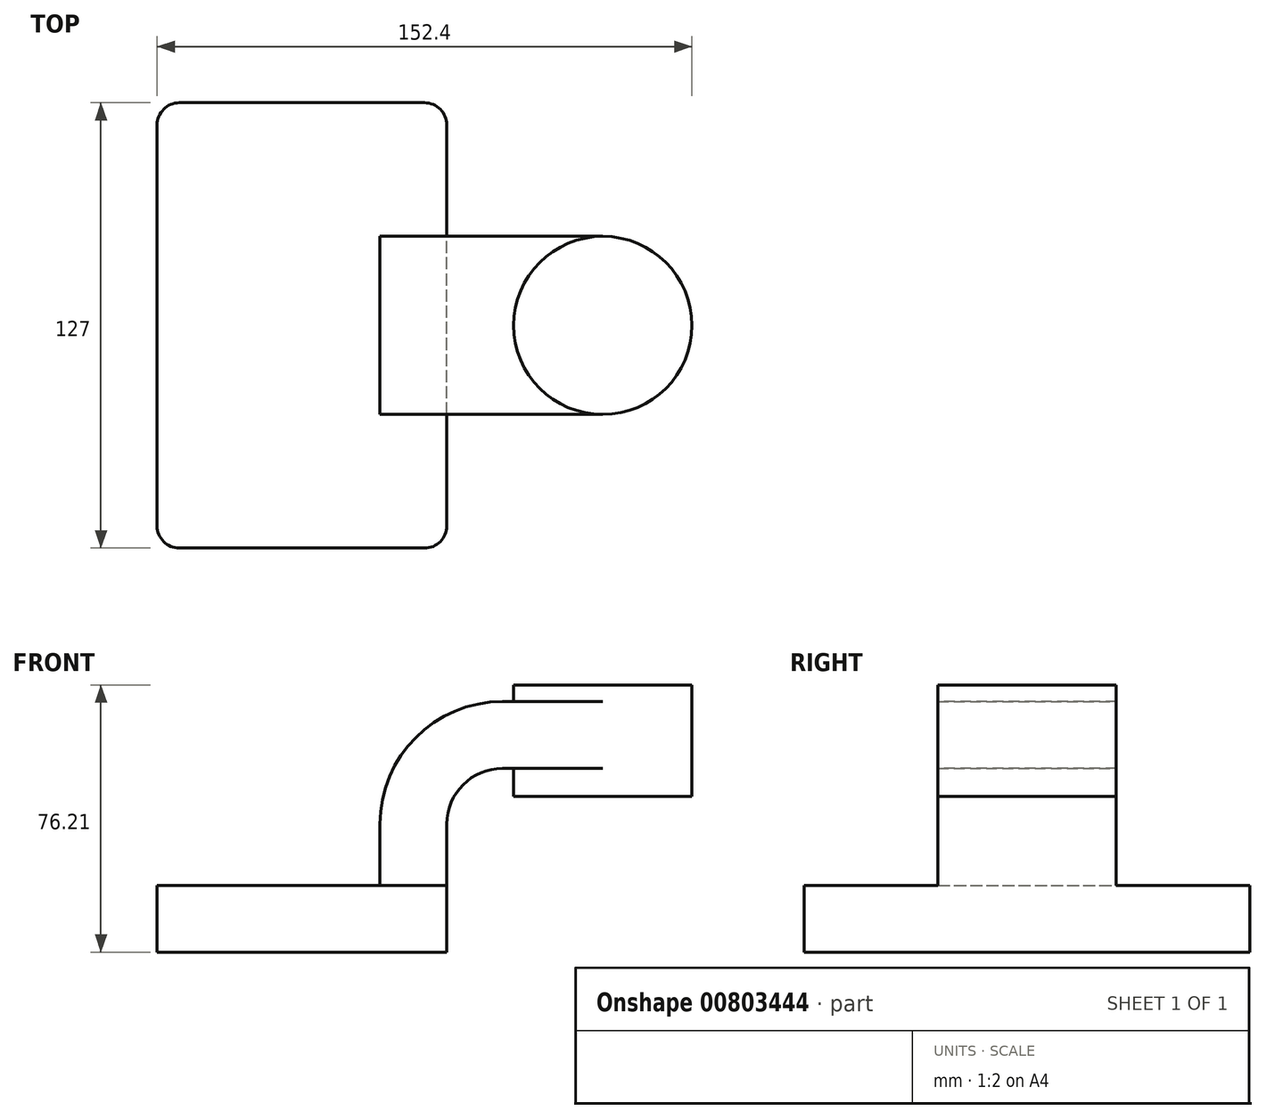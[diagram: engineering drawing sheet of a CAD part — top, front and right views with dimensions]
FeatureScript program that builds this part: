
annotation { "Feature Type Name" : "Feature", "Feature Type Description" : "" }
export const myFeature = defineFeature(function(context is Context, id is Id, definition is map)
    precondition{}
    {
        {
            var Q0;
            Q0=qCreatedBy(makeId("Front.planeOp"),FACE);
            var sketch = newSketch(context, id + "F0", { "sketchPlane" : qUnion([Q0])});
            skLineSegment(sketch, "E0.bottom", {"start": v(41.27, 9.53) * mm, "end": v(-41.28, 9.53) * mm});
            skLineSegment(sketch, "E0.top", {"start": v(41.28, -9.52) * mm, "end": v(-41.27, -9.52) * mm});
            skLineSegment(sketch, "E0.left", {"start": v(41.28, 9.53) * mm, "end": v(41.28, -9.52) * mm});
            skLineSegment(sketch, "E0.right", {"start": v(-41.28, 9.53) * mm, "end": v(-41.27, -9.52) * mm});
            skPoint(sketch, "E0.middle", {"position": v(0, 0) * mm});
            skLineSegment(sketch, "E1.bottom", {"start": v(111.13, 34.93) * mm, "end": v(60.33, 34.93) * mm});
            skLineSegment(sketch, "E1.top", {"start": v(111.13, 66.68) * mm, "end": v(60.33, 66.68) * mm});
            skLineSegment(sketch, "E1.left", {"start": v(111.13, 34.93) * mm, "end": v(111.13, 66.68) * mm});
            skLineSegment(sketch, "E1.right", {"start": v(60.33, 34.92) * mm, "end": v(60.33, 66.68) * mm});
            skPoint(sketch, "E1.middle", {"position": v(85.73, 50.8) * mm});
            skLineSegment(sketch, "E2", {"start": v(41.27, 9.53) * mm, "end": v(41.27, 26.99) * mm});
            skLineSegment(sketch, "E3", {"start": v(57.15, 42.86) * mm, "end": v(85.73, 42.86) * mm});
            skArc(sketch, "E4", {"start": v(41.27, 26.99) * mm, "mid": v(45.92, 38.21) * mm, "end": v(57.15, 42.86) * mm});
            skLineSegment(sketch, "E5.0", {"start": v(57.15, 61.91) * mm, "end": v(85.73, 61.91) * mm});
            skArc(sketch, "E5.1", {"start": v(22.22, 26.99) * mm, "mid": v(32.45, 51.68) * mm, "end": v(57.15, 61.91) * mm});
            skLineSegment(sketch, "E5.2", {"start": v(22.22, 9.53) * mm, "end": v(22.22, 26.99) * mm});
            skPoint(sketch, "E6", {"position": v(85.73, 66.68) * mm});
            skLineSegment(sketch, "E7", {"start": v(85.73, 66.68) * mm, "end": v(85.73, 34.93) * mm});
            skFitSpline(sketch, "E8", {"points": [v(-41.28, 9.52) * mm, v(57.15, 61.91) * mm], "startDerivative": vector(2, 100.61) * mm, "endDerivative": vector(143.14, -0.83) * mm});
            skSolve(sketch);
        }
        {
            var Q0;
            Q0=makeQuery(id+"F0.imprint","IMPRINT",FACE,{"disambiguationData":[TD([[makeQuery(id+"F0.imprint","IMPRINT",EDGE,{"derivedFrom":sQuery(id+"F0.wireOp",EDGE,"E0.top")}),-1.0]])]});
            extrude(context, id + "F1", {"entities" : qUnion([Q0]), "endBound" : BoundingType.SYMMETRIC, "depth" : 127 * mm, "offsetDistance" : 25.4 * mm});
        }
        {
            var Q0;
            {var subQ4=sQuery(id+"F0.wireOp",EDGE,"E2");Q0=makeQuery(id+"F0.imprint","IMPRINT",FACE,{"disambiguationData":[TD([[makeQuery(id+"F0.imprint","IMPRINT",EDGE,{"derivedFrom":subQ4}),1.0]])]});}
            var Q1;
            {var subQ0=sQuery(id+"F0.wireOp",EDGE,"E3");var subQ1=sQuery(id+"F0.wireOp",EDGE,"E1.right");var subQ2=makeQuery(id+"F0.imprint","INTERSECT",VERTEX,{"derivedFrom":[subQ1,subQ0]});Q1=makeQuery(id+"F0.imprint","IMPRINT",FACE,{"disambiguationData":[TD([[makeQuery(id+"F0.imprint","IMPRINT",EDGE,{"disambiguationData":[TD([[subQ2,-1.0]])],"derivedFrom":subQ1}),-1.0]])]});}
            extrude(context, id + "F2", {"entities" : qUnion([Q0, Q1]), "operationType" : NewBodyOperationType.ADD, "endBound" : BoundingType.SYMMETRIC, "depth" : 50.8 * mm, "offsetDistance" : 25.4 * mm});
        }
        {
            var Q0;
            Q0=makeQuery(id+"F0.imprint","IMPRINT",FACE,{"disambiguationData":[TD([[makeQuery(id+"F0.imprint","IMPRINT",EDGE,{"derivedFrom":sQuery(id+"F0.wireOp",EDGE,"E5.1")}),1.0]])]});
            extrude(context, id + "F3", {"entities" : qUnion([Q0]), "operationType" : NewBodyOperationType.ADD, "endBound" : BoundingType.SYMMETRIC, "depth" : 15.88 * mm, "offsetDistance" : 25.4 * mm});
        }
        {
            var Q0;
            {var subQ4=sQuery(id+"F0.wireOp",EDGE,"E1.left");Q0=makeQuery(id+"F0.imprint","IMPRINT",FACE,{"disambiguationData":[TD([[makeQuery(id+"F0.imprint","IMPRINT",EDGE,{"derivedFrom":subQ4}),1.0]])]});}
            var Q1;
            Q1=sQuery(id+"F0.wireOp",EDGE,"E7");
            revolve(context, id + "F4", {"operationType" : NewBodyOperationType.ADD, "surfaceOperationType" : NewSurfaceOperationType.NEW, "entities" : qUnion([Q0]), "axis" : qUnion([Q1]), "revolveType" : RevolveType.FULL});
        }
        {
            var Q0;
            Q0=makeQuery(id+"F1.opExtrude","CAP_EDGE",EDGE,{"disambiguationData":[OSD([sQuery(id+"F0.wireOp",EDGE,"E0.left")])],"isStart":false});
            var Q1;
            Q1=makeQuery(id+"F1.opExtrude","CAP_EDGE",EDGE,{"disambiguationData":[OSD([sQuery(id+"F0.wireOp",EDGE,"E0.right")])],"isStart":false});
            var Q2;
            Q2=makeQuery(id+"F1.opExtrude","CAP_EDGE",EDGE,{"disambiguationData":[OSD([sQuery(id+"F0.wireOp",EDGE,"E0.right")])],"isStart":true});
            var Q3;
            Q3=makeQuery(id+"F1.opExtrude","CAP_EDGE",EDGE,{"disambiguationData":[OSD([sQuery(id+"F0.wireOp",EDGE,"E0.left")])],"isStart":true});
            fillet(context, id + "F5", {"entities" : qUnion([Q0, Q1, Q2, Q3]), "radius" : 6.35 * mm, "tangentPropagation" : true, "allowEdgeOverflow" : false});
        }
    });
